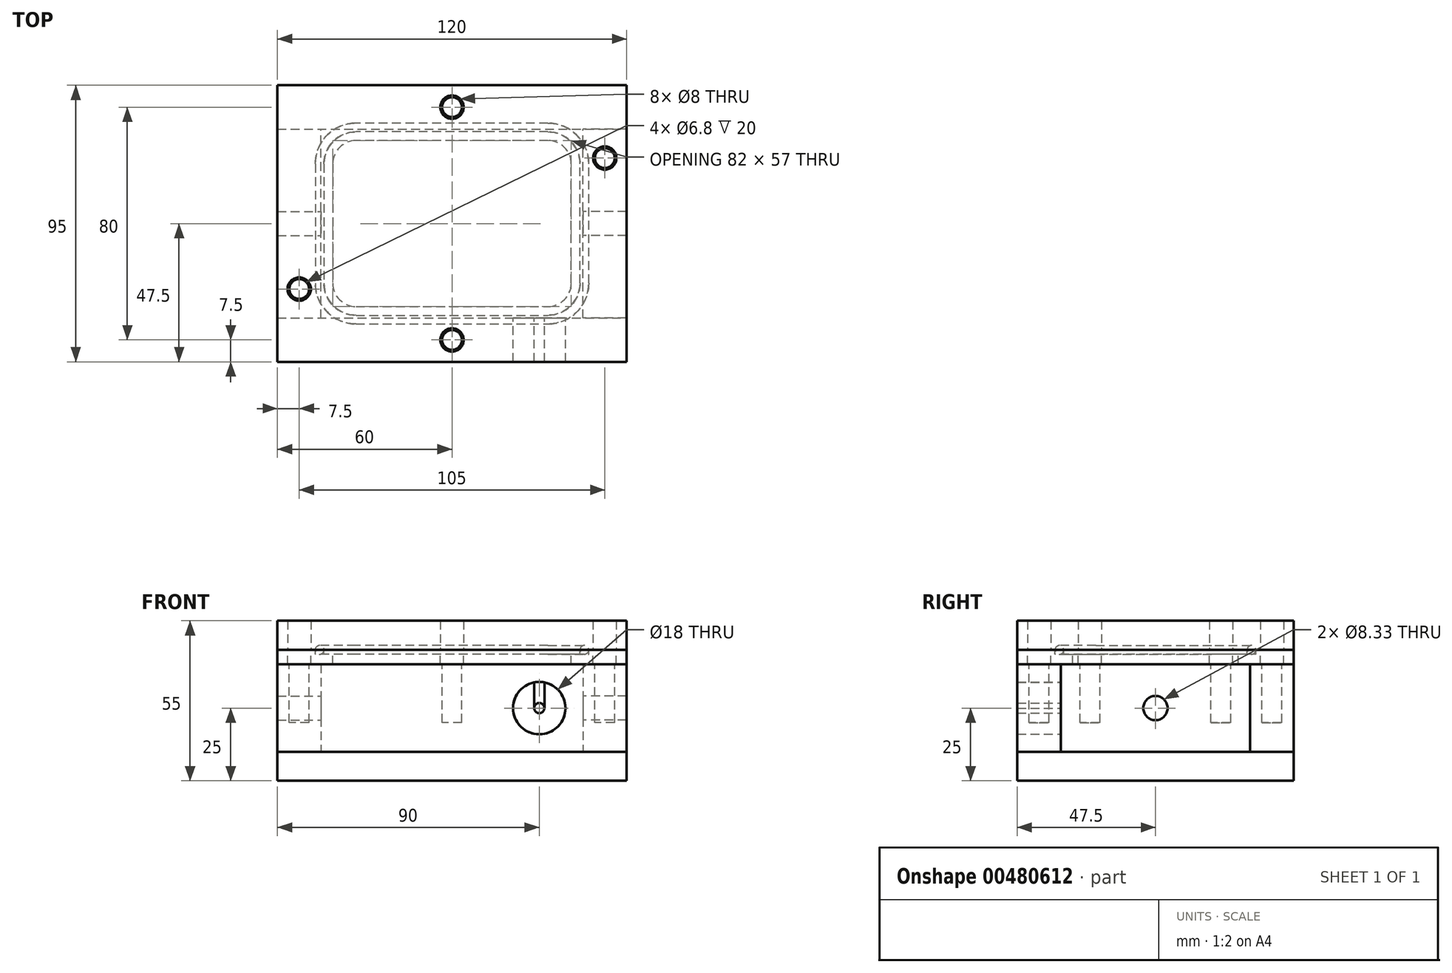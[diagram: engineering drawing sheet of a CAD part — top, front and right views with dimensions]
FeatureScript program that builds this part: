
annotation { "Feature Type Name" : "Feature", "Feature Type Description" : "" }
export const myFeature = defineFeature(function(context is Context, id is Id, definition is map)
    precondition{}
    {
        {
            var Q0;
            Q0=qCreatedBy(makeId("Top.planeOp"),FACE);
            var sketch = newSketch(context, id + "F0", { "sketchPlane" : qUnion([Q0])});
            skLineSegment(sketch, "E0.bottom", {"start": v(-60, 32.5) * mm, "end": v(60, 32.5) * mm});
            skLineSegment(sketch, "E0.top", {"start": v(-60, -32.5) * mm, "end": v(60, -32.5) * mm});
            skLineSegment(sketch, "E0.left", {"start": v(-45, 32.5) * mm, "end": v(-45, -32.5) * mm});
            skLineSegment(sketch, "E0.right", {"start": v(45, 32.5) * mm, "end": v(45, -32.5) * mm});
            skLineSegment(sketch, "E1", {"start": v(-45, 0) * mm, "end": v(45, 0) * mm, "construction": true});
            skLineSegment(sketch, "E2", {"start": v(0, -32.5) * mm, "end": v(0, 32.5) * mm, "construction": true});
            skLineSegment(sketch, "E3.0", {"start": v(-60, 47.5) * mm, "end": v(60, 47.5) * mm});
            skLineSegment(sketch, "E3.1", {"start": v(-60, 47.5) * mm, "end": v(-60, -47.5) * mm});
            skLineSegment(sketch, "E3.2", {"start": v(-60, -47.5) * mm, "end": v(60, -47.5) * mm});
            skLineSegment(sketch, "E3.3", {"start": v(60, 47.5) * mm, "end": v(60, -47.5) * mm});
            skCircle(sketch, "E4", {"center": v(0, 40) * mm, "radius": 3.4 * mm});
            skCircle(sketch, "E5", {"center": v(0, -40) * mm, "radius": 3.4 * mm});
            skCircle(sketch, "E6", {"center": v(52.5, 22.5) * mm, "radius": 3.4 * mm});
            skCircle(sketch, "E7", {"center": v(-52.5, -22.5) * mm, "radius": 3.4 * mm});
            skSolve(sketch);
        }
        {
            var Q0;
            Q0=qCreatedBy(makeId("Top.planeOp"),FACE);
            cPlane(context, id + "F1", {"entities" : qUnion([Q0]), "cplaneType" : CPlaneType.OFFSET, "offset" : 15 * mm, "width" : 150 * mm, "height" : 150 * mm});
        }
        {
            var Q0;
            Q0=qCreatedBy(makeId("Top.planeOp"),FACE);
            cPlane(context, id + "F2", {"entities" : qUnion([Q0]), "cplaneType" : CPlaneType.OFFSET, "offset" : 15 * mm, "oppositeDirection" : true, "width" : 150 * mm, "height" : 150 * mm});
        }
        {
            var Q0;
            Q0=qCreatedBy(id+"F1.planeOp",FACE);
            var sketch = newSketch(context, id + "F3", { "sketchPlane" : qUnion([Q0])});
            skLineSegment(sketch, "E8.0", {"start": v(-45, 32.5) * mm, "end": v(-45, -32.5) * mm, "construction": true});
            skLineSegment(sketch, "E9.0", {"start": v(-45, 32.5) * mm, "end": v(45, 32.5) * mm, "construction": true});
            skLineSegment(sketch, "E10.0", {"start": v(45, 32.5) * mm, "end": v(45, -32.5) * mm, "construction": true});
            skLineSegment(sketch, "E11.0", {"start": v(-45, -32.5) * mm, "end": v(45, -32.5) * mm, "construction": true});
            skPoint(sketch, "E12.orphan", {"position": v(-60, 32.5) * mm});
            skPoint(sketch, "E13.orphan", {"position": v(-60, -32.5) * mm});
            skPoint(sketch, "E14.orphan", {"position": v(60, -32.5) * mm});
            skPoint(sketch, "E15.orphan", {"position": v(60, 32.5) * mm});
            skLineSegment(sketch, "E16.0", {"start": v(41, -20.5) * mm, "end": v(41, 20.5) * mm});
            skLineSegment(sketch, "E16.1", {"start": v(-33, -28.5) * mm, "end": v(33, -28.5) * mm});
            skLineSegment(sketch, "E16.2", {"start": v(-41, 20.5) * mm, "end": v(-41, -20.5) * mm});
            skLineSegment(sketch, "E16.3", {"start": v(33, 28.5) * mm, "end": v(-33, 28.5) * mm});
            skPoint(sketch, "E17.visualSharp", {"position": v(-41, 28.5) * mm});
            skArc(sketch, "E17.filletArc", {"start": v(-33, 28.5) * mm, "mid": v(-38.66, 26.16) * mm, "end": v(-41, 20.5) * mm});
            skPoint(sketch, "E18.visualSharp", {"position": v(-41, -28.5) * mm});
            skArc(sketch, "E18.filletArc", {"start": v(-41, -20.5) * mm, "mid": v(-38.66, -26.16) * mm, "end": v(-33, -28.5) * mm});
            skPoint(sketch, "E19.visualSharp", {"position": v(41, -28.5) * mm});
            skArc(sketch, "E19.filletArc", {"start": v(33, -28.5) * mm, "mid": v(38.66, -26.16) * mm, "end": v(41, -20.5) * mm});
            skPoint(sketch, "E20.visualSharp", {"position": v(41, 28.5) * mm});
            skArc(sketch, "E20.filletArc", {"start": v(41, 20.5) * mm, "mid": v(38.66, 26.16) * mm, "end": v(33, 28.5) * mm});
            skLineSegment(sketch, "E21.0", {"start": v(33, 31.5) * mm, "end": v(-33, 31.5) * mm});
            skArc(sketch, "E21.1", {"start": v(44, 20.5) * mm, "mid": v(40.78, 28.28) * mm, "end": v(33, 31.5) * mm});
            skArc(sketch, "E21.2", {"start": v(-33, 31.5) * mm, "mid": v(-40.78, 28.28) * mm, "end": v(-44, 20.5) * mm});
            skLineSegment(sketch, "E21.3", {"start": v(44, -20.5) * mm, "end": v(44, 20.5) * mm});
            skLineSegment(sketch, "E21.4", {"start": v(-44, 20.5) * mm, "end": v(-44, -20.5) * mm});
            skArc(sketch, "E21.5", {"start": v(-44, -20.5) * mm, "mid": v(-40.78, -28.28) * mm, "end": v(-33, -31.5) * mm});
            skLineSegment(sketch, "E21.6", {"start": v(-33, -31.5) * mm, "end": v(33, -31.5) * mm});
            skArc(sketch, "E21.7", {"start": v(33, -31.5) * mm, "mid": v(40.78, -28.28) * mm, "end": v(44, -20.5) * mm});
            skLineSegment(sketch, "E22.0", {"start": v(33, 34.5) * mm, "end": v(-33, 34.5) * mm});
            skArc(sketch, "E22.1", {"start": v(47, 20.5) * mm, "mid": v(42.9, 30.4) * mm, "end": v(33, 34.5) * mm});
            skArc(sketch, "E22.2", {"start": v(-33, 34.5) * mm, "mid": v(-42.9, 30.4) * mm, "end": v(-47, 20.5) * mm});
            skLineSegment(sketch, "E22.3", {"start": v(47, -20.5) * mm, "end": v(47, 20.5) * mm});
            skLineSegment(sketch, "E22.4", {"start": v(-47, 20.5) * mm, "end": v(-47, -20.5) * mm});
            skArc(sketch, "E22.5", {"start": v(-47, -20.5) * mm, "mid": v(-42.9, -30.4) * mm, "end": v(-33, -34.5) * mm});
            skLineSegment(sketch, "E22.6", {"start": v(-33, -34.5) * mm, "end": v(33, -34.5) * mm});
            skArc(sketch, "E22.7", {"start": v(33, -34.5) * mm, "mid": v(42.9, -30.4) * mm, "end": v(47, -20.5) * mm});
            skCircle(sketch, "E23.0", {"center": v(0, 40) * mm, "radius": 4 * mm});
            skCircle(sketch, "E24.0", {"center": v(52.5, 22.5) * mm, "radius": 4 * mm});
            skCircle(sketch, "E25.0", {"center": v(0, -40) * mm, "radius": 4 * mm});
            skCircle(sketch, "E26.0", {"center": v(-52.5, -22.5) * mm, "radius": 4 * mm});
            skSolve(sketch);
        }
        {
            var Q0;
            Q0=qCreatedBy(id+"F1.planeOp",FACE);
            cPlane(context, id + "F4", {"entities" : qUnion([Q0]), "cplaneType" : CPlaneType.OFFSET, "offset" : 5 * mm, "width" : 150 * mm, "height" : 150 * mm});
        }
        {
            var Q0;
            Q0=qCreatedBy(makeId("Front.planeOp"),FACE);
            cPlane(context, id + "F5", {"entities" : qUnion([Q0]), "cplaneType" : CPlaneType.OFFSET, "offset" : (65 / 2) * mm, "width" : 150 * mm, "height" : 150 * mm});
        }
        {
            var Q0;
            Q0=qCreatedBy(id+"F5.planeOp",FACE);
            var sketch = newSketch(context, id + "F6", { "sketchPlane" : qUnion([Q0])});
            skLineSegment(sketch, "E27.bottom", {"start": v(-60, 15) * mm, "end": v(60, 15) * mm});
            skLineSegment(sketch, "E27.top", {"start": v(-60, -15) * mm, "end": v(60, -15) * mm});
            skLineSegment(sketch, "E27.left", {"start": v(-60, 15) * mm, "end": v(-60, -15) * mm});
            skLineSegment(sketch, "E27.right", {"start": v(60, 15) * mm, "end": v(60, -15) * mm});
            skLineSegment(sketch, "E28.0", {"start": v(-60, 0) * mm, "end": v(60, 0) * mm, "construction": true});
            skPoint(sketch, "E29.0", {"position": v(45, 0) * mm});
            skCircle(sketch, "E30", {"center": v(30, 0) * mm, "radius": 9 * mm});
            skSolve(sketch);
        }
        {
            var Q0;
            Q0=qCreatedBy(makeId("Right.planeOp"),FACE);
            var Q1;
            Q1=sQuery(id+"F3.wireOp",EDGE,"E8.0");
            cPlane(context, id + "F7", {"entities" : qUnion([Q0, Q1]), "cplaneType" : CPlaneType.LINE_ANGLE, "offset" : 25 * mm, "angle" : 0 * degree, "width" : 150 * mm, "height" : 150 * mm});
        }
        {
            var Q0;
            Q0=qCreatedBy(id+"F7.planeOp",FACE);
            var sketch = newSketch(context, id + "F8", { "sketchPlane" : qUnion([Q0])});
            skPoint(sketch, "E31.0", {"position": v(32.5, 15) * mm});
            skPoint(sketch, "E32.0", {"position": v(-32.5, 15) * mm});
            skLineSegment(sketch, "E33.bottom", {"start": v(-32.5, 15) * mm, "end": v(32.5, 15) * mm});
            skLineSegment(sketch, "E33.top", {"start": v(-32.5, -15) * mm, "end": v(32.5, -15) * mm});
            skLineSegment(sketch, "E33.left", {"start": v(-32.5, 15) * mm, "end": v(-32.5, -15) * mm});
            skLineSegment(sketch, "E33.right", {"start": v(32.5, 15) * mm, "end": v(32.5, -15) * mm});
            skLineSegment(sketch, "E34.0", {"start": v(-32.5, 0) * mm, "end": v(32.5, 0) * mm, "construction": true});
            skCircle(sketch, "E35", {"center": v(0, 0) * mm, "radius": 4.17 * mm});
            skSolve(sketch);
        }
        {
            var Q0;
            Q0=qCreatedBy(id+"F2.planeOp",FACE);
            var sketch = newSketch(context, id + "F9", { "sketchPlane" : qUnion([Q0])});
            skLineSegment(sketch, "E36.0", {"start": v(-60, 47.5) * mm, "end": v(60, 47.5) * mm});
            skLineSegment(sketch, "E37.0", {"start": v(-60, 47.5) * mm, "end": v(-60, -47.5) * mm});
            skLineSegment(sketch, "E38.0", {"start": v(-60, -47.5) * mm, "end": v(60, -47.5) * mm});
            skLineSegment(sketch, "E39.0", {"start": v(60, 47.5) * mm, "end": v(60, -47.5) * mm});
            skSolve(sketch);
        }
        {
            var Q0;
            Q0 = qSketchRegion(id + "F9", true);
            extrude(context, id + "F10", {"entities" : qUnion([Q0]), "oppositeDirection" : true, "depth" : 10 * mm});
        }
        {
            var Q0;
            Q0=qCreatedBy(id+"F7.planeOp",FACE);
            var sketch = newSketch(context, id + "F11", { "sketchPlane" : qUnion([Q0])});
            skLineSegment(sketch, "E40.0.0", {"start": v(-32.5, 15) * mm, "end": v(-32.5, -15) * mm});
            skLineSegment(sketch, "E40.0.1", {"start": v(-32.5, -15) * mm, "end": v(32.5, -15) * mm});
            skLineSegment(sketch, "E40.0.2", {"start": v(32.5, -15) * mm, "end": v(32.5, 15) * mm});
            skLineSegment(sketch, "E40.0.3", {"start": v(32.5, 15) * mm, "end": v(-32.5, 15) * mm});
            skCircle(sketch, "E41.0", {"center": v(0, 0) * mm, "radius": 4.17 * mm});
            skSolve(sketch);
        }
        {
            var Q0;
            Q0 = qSketchRegion(id + "F11", true);
            extrude(context, id + "F12", {"entities" : qUnion([Q0]), "depth" : 15 * mm});
        }
        {
            var Q0;
            Q0=makeQuery(id+"F12.opExtrude","SWEPT_BODY",BODY,{"disambiguationData":[OSD([sQuery(id+"F11.wireOp",EDGE,"E40.0.0"),sQuery(id+"F11.wireOp",EDGE,"E40.0.1"),sQuery(id+"F11.wireOp",EDGE,"E40.0.2"),sQuery(id+"F11.wireOp",EDGE,"E40.0.3"),sQuery(id+"F11.wireOp",EDGE,"E41.0")])]});
            var Q1;
            Q1=qCreatedBy(makeId("Right.planeOp"),FACE);
            mirror(context, id + "F13", {"entities" : qUnion([Q0]), "mirrorPlane" : qUnion([Q1])});
        }
        {
            var Q0;
            Q0=makeQuery(id+"F6.imprint","IMPRINT",FACE,{"disambiguationData":[TD([[makeQuery(id+"F6.imprint","IMPRINT",EDGE,{"derivedFrom":sQuery(id+"F6.wireOp",EDGE,"E27.bottom")}),-1.0]])]});
            var Q1;
            Q1=makeQuery(id+"F6.imprint","IMPRINT",FACE,{"disambiguationData":[TD([[makeQuery(id+"F6.imprint","IMPRINT",EDGE,{"derivedFrom":sQuery(id+"F6.wireOp",EDGE,"E30")}),1.0]])]});
            extrude(context, id + "F14", {"entities" : qUnion([Q0, Q1]), "depth" : 15 * mm});
        }
        {
            var Q0;
            Q0=makeQuery(id+"F14.opExtrude","SWEPT_BODY",BODY,{"disambiguationData":[OSD([sQuery(id+"F6.wireOp",EDGE,"E27.bottom"),sQuery(id+"F6.wireOp",EDGE,"E27.top"),sQuery(id+"F6.wireOp",EDGE,"E27.left"),sQuery(id+"F6.wireOp",EDGE,"E27.right")])]});
            var Q1;
            Q1=qCreatedBy(makeId("Front.planeOp"),FACE);
            mirror(context, id + "F15", {"entities" : qUnion([Q0]), "mirrorPlane" : qUnion([Q1])});
        }
        {
            var Q0;
            Q0=qCreatedBy(id+"F1.planeOp",FACE);
            var sketch = newSketch(context, id + "F16", { "sketchPlane" : qUnion([Q0])});
            skCircle(sketch, "E42.0", {"center": v(-52.5, -22.5) * mm, "radius": 3.4 * mm});
            skSolve(sketch);
        }
        {
            var Q0;
            Q0 = qSketchRegion(id + "F16", true);
            extrude(context, id + "F17", {"entities" : qUnion([Q0]), "operationType" : NewBodyOperationType.REMOVE, "oppositeDirection" : true, "depth" : 20 * mm});
        }
        {
            var Q0;
            Q0=qCreatedBy(id+"F1.planeOp",FACE);
            var sketch = newSketch(context, id + "F18", { "sketchPlane" : qUnion([Q0])});
            skCircle(sketch, "E43.0", {"center": v(0, -40) * mm, "radius": 3.4 * mm});
            skSolve(sketch);
        }
        {
            var Q0;
            Q0 = qSketchRegion(id + "F18", true);
            extrude(context, id + "F19", {"entities" : qUnion([Q0]), "operationType" : NewBodyOperationType.REMOVE, "oppositeDirection" : true, "depth" : 20 * mm});
        }
        {
            var Q0;
            Q0=qCreatedBy(id+"F1.planeOp",FACE);
            var sketch = newSketch(context, id + "F20", { "sketchPlane" : qUnion([Q0])});
            skCircle(sketch, "E44.0", {"center": v(52.5, 22.5) * mm, "radius": 3.4 * mm});
            skSolve(sketch);
        }
        {
            var Q0;
            Q0 = qSketchRegion(id + "F20", true);
            extrude(context, id + "F21", {"entities" : qUnion([Q0]), "operationType" : NewBodyOperationType.REMOVE, "oppositeDirection" : true, "depth" : 20 * mm});
        }
        {
            var Q0;
            Q0=qCreatedBy(id+"F1.planeOp",FACE);
            var sketch = newSketch(context, id + "F22", { "sketchPlane" : qUnion([Q0])});
            skCircle(sketch, "E45.0", {"center": v(0, 40) * mm, "radius": 3.4 * mm});
            skSolve(sketch);
        }
        {
            var Q0;
            Q0 = qSketchRegion(id + "F22", true);
            extrude(context, id + "F23", {"entities" : qUnion([Q0]), "operationType" : NewBodyOperationType.REMOVE, "oppositeDirection" : true, "depth" : 20 * mm});
        }
        {
            var Q0;
            Q0=qCreatedBy(id+"F5.planeOp",FACE);
            var sketch = newSketch(context, id + "F24", { "sketchPlane" : qUnion([Q0])});
            skCircle(sketch, "E46.0", {"center": v(30, 0) * mm, "radius": 9 * mm});
            skSolve(sketch);
        }
        {
            var Q0;
            Q0 = qSketchRegion(id + "F24", true);
            extrude(context, id + "F25", {"entities" : qUnion([Q0]), "operationType" : NewBodyOperationType.REMOVE, "depth" : 15 * mm});
        }
        {
            var Q0;
            Q0=qCreatedBy(id+"F4.planeOp",FACE);
            var sketch = newSketch(context, id + "F26", { "sketchPlane" : qUnion([Q0])});
            skLineSegment(sketch, "E47.0", {"start": v(-60, 47.5) * mm, "end": v(-60, -47.5) * mm});
            skLineSegment(sketch, "E48.0", {"start": v(-60, 47.5) * mm, "end": v(60, 47.5) * mm});
            skLineSegment(sketch, "E49.0", {"start": v(60, 47.5) * mm, "end": v(60, -47.5) * mm});
            skLineSegment(sketch, "E50.0", {"start": v(-60, -47.5) * mm, "end": v(60, -47.5) * mm});
            skArc(sketch, "E51.0.0", {"start": v(-33, 28.5) * mm, "mid": v(-38.66, 26.16) * mm, "end": v(-41, 20.5) * mm});
            skLineSegment(sketch, "E51.0.1", {"start": v(-41, 20.5) * mm, "end": v(-41, -20.5) * mm});
            skArc(sketch, "E51.0.2", {"start": v(-41, -20.5) * mm, "mid": v(-38.66, -26.16) * mm, "end": v(-33, -28.5) * mm});
            skLineSegment(sketch, "E51.0.3", {"start": v(-33, -28.5) * mm, "end": v(33, -28.5) * mm});
            skArc(sketch, "E51.0.4", {"start": v(33, -28.5) * mm, "mid": v(38.66, -26.16) * mm, "end": v(41, -20.5) * mm});
            skLineSegment(sketch, "E51.0.5", {"start": v(41, -20.5) * mm, "end": v(41, 20.5) * mm});
            skArc(sketch, "E51.0.6", {"start": v(41, 20.5) * mm, "mid": v(38.66, 26.16) * mm, "end": v(33, 28.5) * mm});
            skLineSegment(sketch, "E51.0.7", {"start": v(33, 28.5) * mm, "end": v(-33, 28.5) * mm});
            skSolve(sketch);
        }
        {
            var Q0;
            Q0 = qSketchRegion(id + "F26", true);
            extrude(context, id + "F27", {"entities" : qUnion([Q0]), "oppositeDirection" : true, "depth" : 5 * mm});
        }
        {
            var Q0;
            Q0=qCreatedBy(id+"F4.planeOp",FACE);
            var sketch = newSketch(context, id + "F28", { "sketchPlane" : qUnion([Q0])});
            skArc(sketch, "E52.0", {"start": v(-33, 31.5) * mm, "mid": v(-40.78, 28.28) * mm, "end": v(-44, 20.5) * mm});
            skArc(sketch, "E53.0", {"start": v(-33, 34.5) * mm, "mid": v(-42.9, 30.4) * mm, "end": v(-47, 20.5) * mm});
            skLineSegment(sketch, "E54.0", {"start": v(33, 34.5) * mm, "end": v(-33, 34.5) * mm});
            skLineSegment(sketch, "E55.0", {"start": v(33, 31.5) * mm, "end": v(-33, 31.5) * mm});
            skArc(sketch, "E56.0", {"start": v(47, 20.5) * mm, "mid": v(42.9, 30.4) * mm, "end": v(33, 34.5) * mm});
            skPoint(sketch, "E57.0", {"position": v(40.78, 28.28) * mm});
            skArc(sketch, "E58.0", {"start": v(44, 20.5) * mm, "mid": v(40.78, 28.28) * mm, "end": v(33, 31.5) * mm});
            skLineSegment(sketch, "E59.0", {"start": v(44, -20.5) * mm, "end": v(44, 20.5) * mm});
            skArc(sketch, "E60.0", {"start": v(33, -31.5) * mm, "mid": v(40.78, -28.28) * mm, "end": v(44, -20.5) * mm});
            skLineSegment(sketch, "E61.0", {"start": v(-33, -31.5) * mm, "end": v(33, -31.5) * mm});
            skArc(sketch, "E62.0", {"start": v(-44, -20.5) * mm, "mid": v(-40.78, -28.28) * mm, "end": v(-33, -31.5) * mm});
            skLineSegment(sketch, "E63.0", {"start": v(-44, 20.5) * mm, "end": v(-44, -20.5) * mm});
            skLineSegment(sketch, "E64.0", {"start": v(-47, 20.5) * mm, "end": v(-47, -20.5) * mm});
            skArc(sketch, "E65.0", {"start": v(-47, -20.5) * mm, "mid": v(-42.9, -30.4) * mm, "end": v(-33, -34.5) * mm});
            skLineSegment(sketch, "E66.0", {"start": v(-33, -34.5) * mm, "end": v(33, -34.5) * mm});
            skArc(sketch, "E67.0", {"start": v(33, -34.5) * mm, "mid": v(42.9, -30.4) * mm, "end": v(47, -20.5) * mm});
            skLineSegment(sketch, "E68.0", {"start": v(47, -20.5) * mm, "end": v(47, 20.5) * mm});
            skSolve(sketch);
        }
        {
            var Q0;
            Q0 = qSketchRegion(id + "F28", true);
            extrude(context, id + "F29", {"entities" : qUnion([Q0]), "operationType" : NewBodyOperationType.REMOVE, "oppositeDirection" : true, "depth" : 1.5 * mm});
        }
        {
            var Q0;
            Q0=qCreatedBy(id+"F4.planeOp",FACE);
            var sketch = newSketch(context, id + "F30", { "sketchPlane" : qUnion([Q0])});
            skCircle(sketch, "E69.0", {"center": v(-52.5, -22.5) * mm, "radius": 4 * mm});
            skCircle(sketch, "E70.0", {"center": v(0, -40) * mm, "radius": 4 * mm});
            skCircle(sketch, "E71.0", {"center": v(52.5, 22.5) * mm, "radius": 4 * mm});
            skCircle(sketch, "E72.0", {"center": v(0, 40) * mm, "radius": 4 * mm});
            skSolve(sketch);
        }
        {
            var Q0;
            Q0 = qSketchRegion(id + "F30", true);
            extrude(context, id + "F31", {"entities" : qUnion([Q0]), "operationType" : NewBodyOperationType.REMOVE, "oppositeDirection" : true, "depth" : 5 * mm});
        }
        {
            var Q0;
            Q0=qCreatedBy(id+"F4.planeOp",FACE);
            var sketch = newSketch(context, id + "F32", { "sketchPlane" : qUnion([Q0])});
            skLineSegment(sketch, "E73.0", {"start": v(-60, 47.5) * mm, "end": v(-60, -47.5) * mm});
            skLineSegment(sketch, "E74.0", {"start": v(-60, -47.5) * mm, "end": v(60, -47.5) * mm});
            skLineSegment(sketch, "E75.0", {"start": v(60, 47.5) * mm, "end": v(60, -47.5) * mm});
            skLineSegment(sketch, "E76.0", {"start": v(-60, 47.5) * mm, "end": v(60, 47.5) * mm});
            skCircle(sketch, "E77.0", {"center": v(0, 40) * mm, "radius": 4 * mm});
            skCircle(sketch, "E78.0", {"center": v(-52.5, -22.5) * mm, "radius": 4 * mm});
            skCircle(sketch, "E79.0", {"center": v(0, -40) * mm, "radius": 4 * mm});
            skCircle(sketch, "E80.0", {"center": v(52.5, 22.5) * mm, "radius": 4 * mm});
            skSolve(sketch);
        }
        {
            var Q0;
            Q0 = qSketchRegion(id + "F32", true);
            extrude(context, id + "F33", {"entities" : qUnion([Q0]), "depth" : 10 * mm});
        }
        {
            var Q0;
            Q0=qCreatedBy(id+"F5.planeOp",FACE);
            var sketch = newSketch(context, id + "F34", { "sketchPlane" : qUnion([Q0])});
            skCircle(sketch, "E81.0", {"center": v(30, 0) * mm, "radius": 9 * mm});
            skCircle(sketch, "E82", {"center": v(30, 0) * mm, "radius": 1.75 * mm});
            skLineSegment(sketch, "E83", {"start": v(28.25, 0) * mm, "end": v(31.75, 0) * mm, "construction": true});
            skLineSegment(sketch, "E84", {"start": v(31.75, 0) * mm, "end": v(31.75, 8.83) * mm});
            skLineSegment(sketch, "E85", {"start": v(28.25, 0) * mm, "end": v(28.25, 8.83) * mm});
            skSolve(sketch);
        }
        {
            var Q0;
            Q0=qCreatedBy(id+"F5.planeOp",FACE);
            var sketch = newSketch(context, id + "F35", { "sketchPlane" : qUnion([Q0])});
            skArc(sketch, "E86.0", {"start": v(28.25, 8.83) * mm, "mid": v(30, -9) * mm, "end": v(31.75, 8.83) * mm});
            skLineSegment(sketch, "E87.0", {"start": v(28.25, 0) * mm, "end": v(28.25, 8.83) * mm});
            skLineSegment(sketch, "E88.0", {"start": v(31.75, 0) * mm, "end": v(31.75, 8.83) * mm});
            skArc(sketch, "E89.0", {"start": v(28.25, 0) * mm, "mid": v(30, -1.75) * mm, "end": v(31.75, 0) * mm});
            skSolve(sketch);
        }
        {
            var Q0;
            Q0 = qSketchRegion(id + "F35", true);
            extrude(context, id + "F36", {"entities" : qUnion([Q0]), "depth" : 15 * mm});
        }
        {
            var Q0;
            Q0=qCreatedBy(id+"F5.planeOp",FACE);
            var sketch = newSketch(context, id + "F37", { "sketchPlane" : qUnion([Q0])});
            skArc(sketch, "E90.0", {"start": v(31.75, 8.83) * mm, "mid": v(30, 9) * mm, "end": v(28.25, 8.83) * mm});
            skLineSegment(sketch, "E91.0", {"start": v(31.75, 0) * mm, "end": v(31.75, 8.83) * mm});
            skLineSegment(sketch, "E92.0", {"start": v(28.25, 0) * mm, "end": v(28.25, 8.83) * mm});
            skArc(sketch, "E93.0", {"start": v(31.75, 0) * mm, "mid": v(30, 1.75) * mm, "end": v(28.25, 0) * mm});
            skSolve(sketch);
        }
        {
            var Q0;
            Q0 = qSketchRegion(id + "F37", true);
            extrude(context, id + "F38", {"entities" : qUnion([Q0]), "depth" : 15 * mm});
        }
        {
            var Q0;
            Q0=qCreatedBy(id+"F4.planeOp",FACE);
            var sketch = newSketch(context, id + "F39", { "sketchPlane" : qUnion([Q0])});
            skLineSegment(sketch, "E94.0", {"start": v(-44, 20.5) * mm, "end": v(-44, -20.5) * mm, "construction": true});
            skLineSegment(sketch, "E95.0", {"start": v(-47, 0) * mm, "end": v(45, 0) * mm, "construction": true});
            skLineSegment(sketch, "E96.0", {"start": v(-47, 20.5) * mm, "end": v(-47, -20.5) * mm, "construction": true});
            skArc(sketch, "E97.0", {"start": v(-33, 33) * mm, "mid": v(-41.84, 29.34) * mm, "end": v(-45.5, 20.5) * mm});
            skLineSegment(sketch, "E97.1", {"start": v(33, 33) * mm, "end": v(-33, 33) * mm});
            skArc(sketch, "E97.2", {"start": v(45.5, 20.5) * mm, "mid": v(41.84, 29.34) * mm, "end": v(33, 33) * mm});
            skArc(sketch, "E97.3", {"start": v(-45.5, -20.5) * mm, "mid": v(-41.84, -29.34) * mm, "end": v(-33, -33) * mm});
            skLineSegment(sketch, "E97.4", {"start": v(-33, -33) * mm, "end": v(33, -33) * mm});
            skArc(sketch, "E97.5", {"start": v(33, -33) * mm, "mid": v(41.84, -29.34) * mm, "end": v(45.5, -20.5) * mm});
            skLineSegment(sketch, "E97.6", {"start": v(45.5, -20.5) * mm, "end": v(45.5, 20.5) * mm});
            skLineSegment(sketch, "E98", {"start": v(-45.5, 0) * mm, "end": v(-45.5, 20.5) * mm});
            skLineSegment(sketch, "E99", {"start": v(-45.5, 0) * mm, "end": v(-45.5, -20.5) * mm});
            skSolve(sketch);
        }
        {
            var Q0;
            Q0=qCreatedBy(makeId("Front.planeOp"),FACE);
            var sketch = newSketch(context, id + "F40", { "sketchPlane" : qUnion([Q0])});
            skCircle(sketch, "E100", {"center": v(-45.5, 20) * mm, "radius": 1.5 * mm});
            skSolve(sketch);
        }
        {
            var Q0;
            Q0 = qSketchRegion(id + "F40", true);
            var Q1;
            Q1 = qConstructionFilter(qBodyType(qCreatedBy(id + "F39" ,EDGE), BodyType.WIRE), ConstructionObject.NO);
            sweep(context, id + "F41", {"profiles" : qUnion([Q0]), "path" : qUnion([Q1])});
        }
    });
